# Revit family: Lighting_Emergency&Security_Linergy_vialed-high-mini-box
name_source: partatom
category: Lighting Fixtures
revit_build: Autodesk Revit 2018 (Build: 20170223_1515(x64)
units: mm (PartAtom-declared; Revit-internal decimal feet)

## family parameters
Cut with Voids When Loaded = No
Host = Face
Light Source = Yes
OmniClass Number = 23.35.47.13
OmniClass Title = Emergency Lighting
Part Type = Normal
Room Calculation Point = No
Round Connector Dimension = Use Diameter
Shared = No

## types (1)
- Default - please load Revit Family Type Catalog
    Apparent Load = 0 VA
    Apparent Load Phase 1 = 0 VA
    Apparent Load Phase 2 = 0 VA
    Apparent Load Phase 3 = 0 VA
    BIMobject category = Emergency & Security
    Battery = Li-FePO4 3,2V 1,5Ah
    Color Filter = 16777215
    Default Elevation = 1219.2 mm  [stored 4 ft]
    Description = LED Emergency lighting luminaire. Ceiling mount. Vialed High ceiling version. Studied for high ceilings applications (over 10m). High lighting performances. Includes symmetrical and asymmetrical optics.
    Design country = Italy
    Detail material = Linergy - Plastic - Polycarbonate Transparent high polished
    Dimming Lamp Color Temperature Shift = <None>
    Duration = 1 h
    Edition number = 1
    Flux M = 355 lm
    Flux N/M = 355 lm
    Function = Rest Mode
    IFC Classification = Light Fixture
    Input power = 5 W
    Installation instructions = https://www.linergy.it
    Insulation class = I
    Lamp type = NM/M
    Main material = Linergy - Plastic - PVC White 9003
    Manufacturer = Linergy
    Manufacturer country = Italy
    Manufacturer name = Linergy
    Material main = PC/ABS
    Material secondary = Electronic & optical components
    Model = VF1201.S
    Number of Poles = 1
    OmniClass Code = 23-35 47 13
    OmniClass Description = Emergency Lighting
    Photometric Web File = generic
    Power supply = 230 Vac
    Product Guid = 40c63400-0822-4f0b-be39-1512d6707c9e
    Product SKU = vialed-high-mini-box
    Product certification = https://www.linergy.it
    Product data url = https://bimobject.com
    Product family = Emergency luminaires
    Product group = Vialed emergency luminaires
    Product name = VIALED HIGH MINI BOX - Emergency lighting luminaire
    Product url = https://www.linergy.it
    Protection degree = IP42
    QR code = https://bimobject.com
    Technical description = https://www.linergy.it
    Tilt Angle = 90.00°
    URL = https://www.linergy.it
    URL - Article page = https://www.linergy.it
    URL - Photometric file (ldt) = https://www.linergy.it
    Voltage = 230 V
    z_visibility_a = No
    z_visibility_s = Yes

note: [stored X ft] marks values corroborated as IEEE doubles in the binary element streams (Revit-internal decimal feet)

## geometry (parser evidence)
native form markers: Blend x28, Sweep x2
no freeform markers — native parametric forms only
